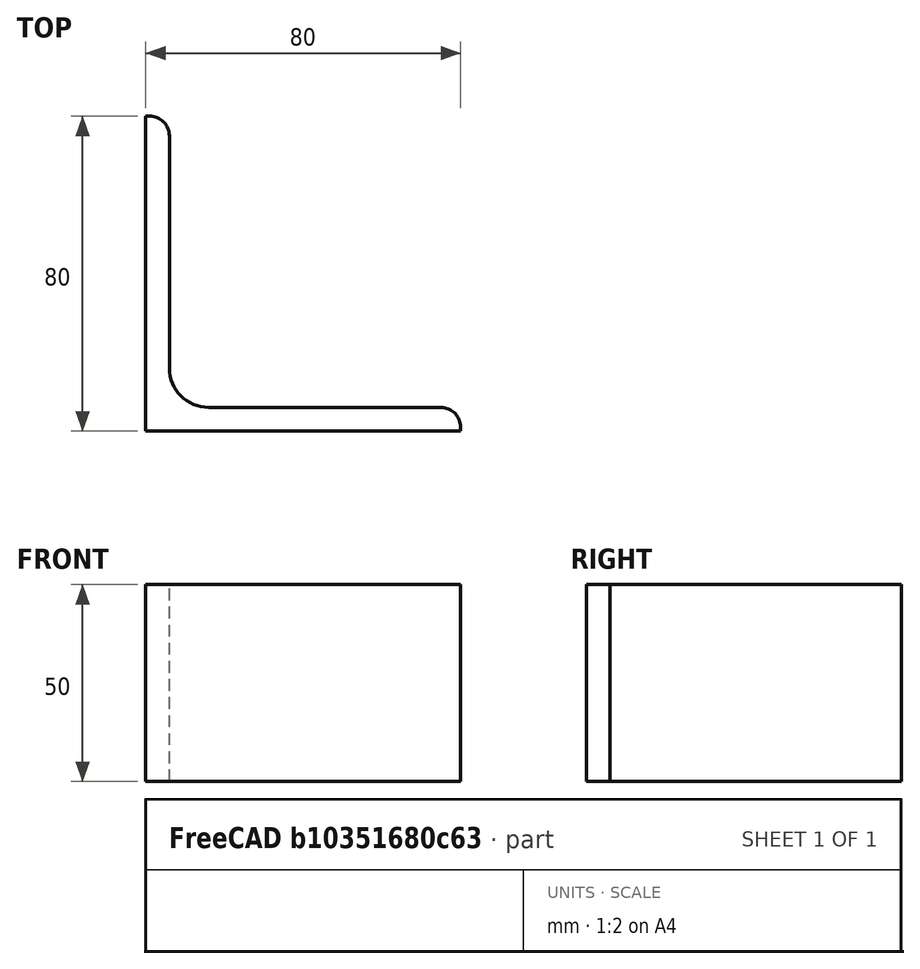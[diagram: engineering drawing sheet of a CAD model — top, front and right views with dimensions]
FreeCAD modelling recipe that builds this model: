
FCSTD DOCUMENT  (FreeCAD 0.15R4671 (Git))
Label: Angle Bar L80x80x6 EN10056 S235JR
License: All rights reserved
LicenseURL: http://en.wikipedia.org/wiki/All_rights_reserved
objects: Sketcher::SketchObject×1, Part::Extrusion×1
note: 2 computed .brp shape members not serialized (recipe doc carries the construction recipe); baked Part::Feature solids carry a one-line shape summary decoded from their .brp

FEATURE [Sketcher::SketchObject] Sketch
  sketch-geometry (9):
    g0: LineSegment StartX=0 StartY=0 StartZ=0 EndX=80 EndY=0 EndZ=0
    g1: LineSegment StartX=80 StartY=0 StartZ=0 EndX=80 EndY=1 EndZ=0
    g2: LineSegment StartX=75 StartY=6 StartZ=0 EndX=16 EndY=6 EndZ=0
    g3: LineSegment StartX=0 StartY=0 StartZ=0 EndX=0 EndY=80 EndZ=0
    g4: LineSegment StartX=0 StartY=80 StartZ=0 EndX=1 EndY=80 EndZ=0
    g5: LineSegment StartX=6 StartY=75 StartZ=0 EndX=6 EndY=16 EndZ=0
    g6: ArcOfCircle CenterX=16 CenterY=16 CenterZ=0 NormalX=0 NormalY=0 NormalZ=1 Radius=10 StartAngle=3.14159 EndAngle=4.71239
    g7: ArcOfCircle CenterX=1 CenterY=75 CenterZ=0 NormalX=0 NormalY=0 NormalZ=1 Radius=5 StartAngle=0 EndAngle=1.5708
    g8: ArcOfCircle CenterX=75 CenterY=1 CenterZ=0 NormalX=0 NormalY=0 NormalZ=1 Radius=5 StartAngle=0 EndAngle=1.5708
  constraints (23):
    c: Coincident(g0,g-1)
    c: Horizontal(g0)
    c: Coincident(g1,g0)
    c: Vertical(g1)
    c: Horizontal(g2)
    c: Coincident(g3,g-1)
    c: Vertical(g3)
    c: Coincident(g4,g3)
    c: Horizontal(g4)
    c: Vertical(g5)
    c: Tangent(g5,g6) = -1.5708
    c: Tangent(g2,g6) = 1.5708
    c: Tangent(g4,g7) = 1.5708
    c: Tangent(g5,g7) = 1.5708
    c: Tangent(g2,g8) = -1.5708
    c: Tangent(g1,g8) = -1.5708
    c: DistanceX(g0) = 80
    c: DistanceY(g3) = 80
    c: DistanceY(g0,g2) = 6
    c: DistanceX(g3,g5) = 6
    c: Radius(g6) = 10
    c: Radius(g8) = 5
    c: Radius(g7) = 5
FEATURE [Part::Extrusion] Extrude  label="Angle Bar L80x80x6 EN10056 S235JR"
  Base = -> Sketch
  Dir = (0,0,50)
  Solid = true
